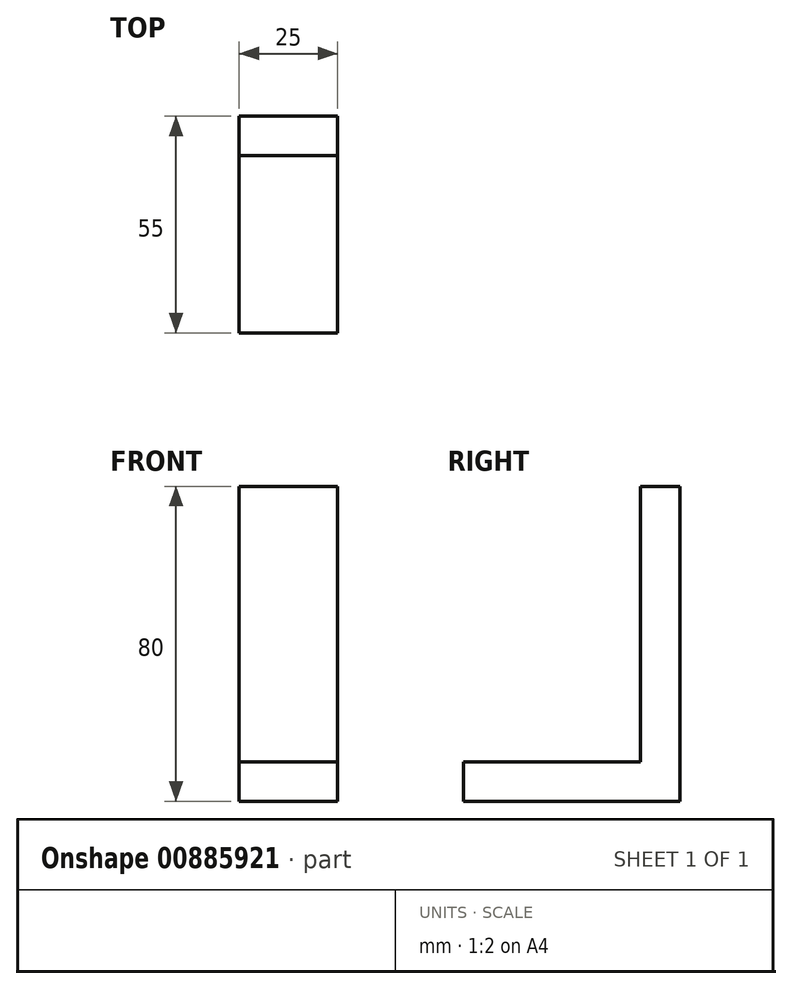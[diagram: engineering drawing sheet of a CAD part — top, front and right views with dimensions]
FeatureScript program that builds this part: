
annotation { "Feature Type Name" : "Feature", "Feature Type Description" : "" }
export const myFeature = defineFeature(function(context is Context, id is Id, definition is map)
    precondition{}
    {
        {
            var Q0;
            Q0=qCreatedBy(makeId("Front.planeOp"),FACE);
            var sketch = newSketch(context, id + "F0", { "sketchPlane" : qUnion([Q0])});
            skLineSegment(sketch, "E0.bottom", {"start": v(-12.5, 40) * mm, "end": v(12.5, 40) * mm});
            skLineSegment(sketch, "E0.top", {"start": v(-12.5, -40) * mm, "end": v(12.5, -40) * mm});
            skLineSegment(sketch, "E0.left", {"start": v(-12.5, 40) * mm, "end": v(-12.5, -40) * mm});
            skLineSegment(sketch, "E0.right", {"start": v(12.5, 40) * mm, "end": v(12.5, -40) * mm});
            skPoint(sketch, "E0.middle", {"position": v(0, 0) * mm});
            skSolve(sketch);
        }
        {
            var Q0;
            Q0 = qSketchRegion(id + "F0", true);
            extrude(context, id + "F1", {"entities" : qUnion([Q0]), "depth" : 10 * mm, "offsetDistance" : 25 * mm});
        }
        {
            var Q0;
            Q0=makeQuery(id+"F1.opExtrude","CAP_FACE",FACE,{"disambiguationData":[OSD([sQuery(id+"F0.wireOp",EDGE,"E0.bottom"),sQuery(id+"F0.wireOp",EDGE,"E0.top"),sQuery(id+"F0.wireOp",EDGE,"E0.left"),sQuery(id+"F0.wireOp",EDGE,"E0.right")])],"isStart":false});
            var sketch = newSketch(context, id + "F2", { "sketchPlane" : qUnion([Q0])});
            skLineSegment(sketch, "E1.bottom", {"start": v(-12.5, -40) * mm, "end": v(12.5, -40) * mm});
            skLineSegment(sketch, "E1.top", {"start": v(-12.5, -30) * mm, "end": v(12.5, -30) * mm});
            skLineSegment(sketch, "E1.left", {"start": v(-12.5, -40) * mm, "end": v(-12.5, -30) * mm});
            skLineSegment(sketch, "E1.right", {"start": v(12.5, -40) * mm, "end": v(12.5, -30) * mm});
            skSolve(sketch);
        }
        {
            var Q0;
            Q0 = qSketchRegion(id + "F2", true);
            extrude(context, id + "F3", {"entities" : qUnion([Q0]), "operationType" : NewBodyOperationType.ADD, "depth" : 45 * mm, "offsetDistance" : 25 * mm});
        }
    });
